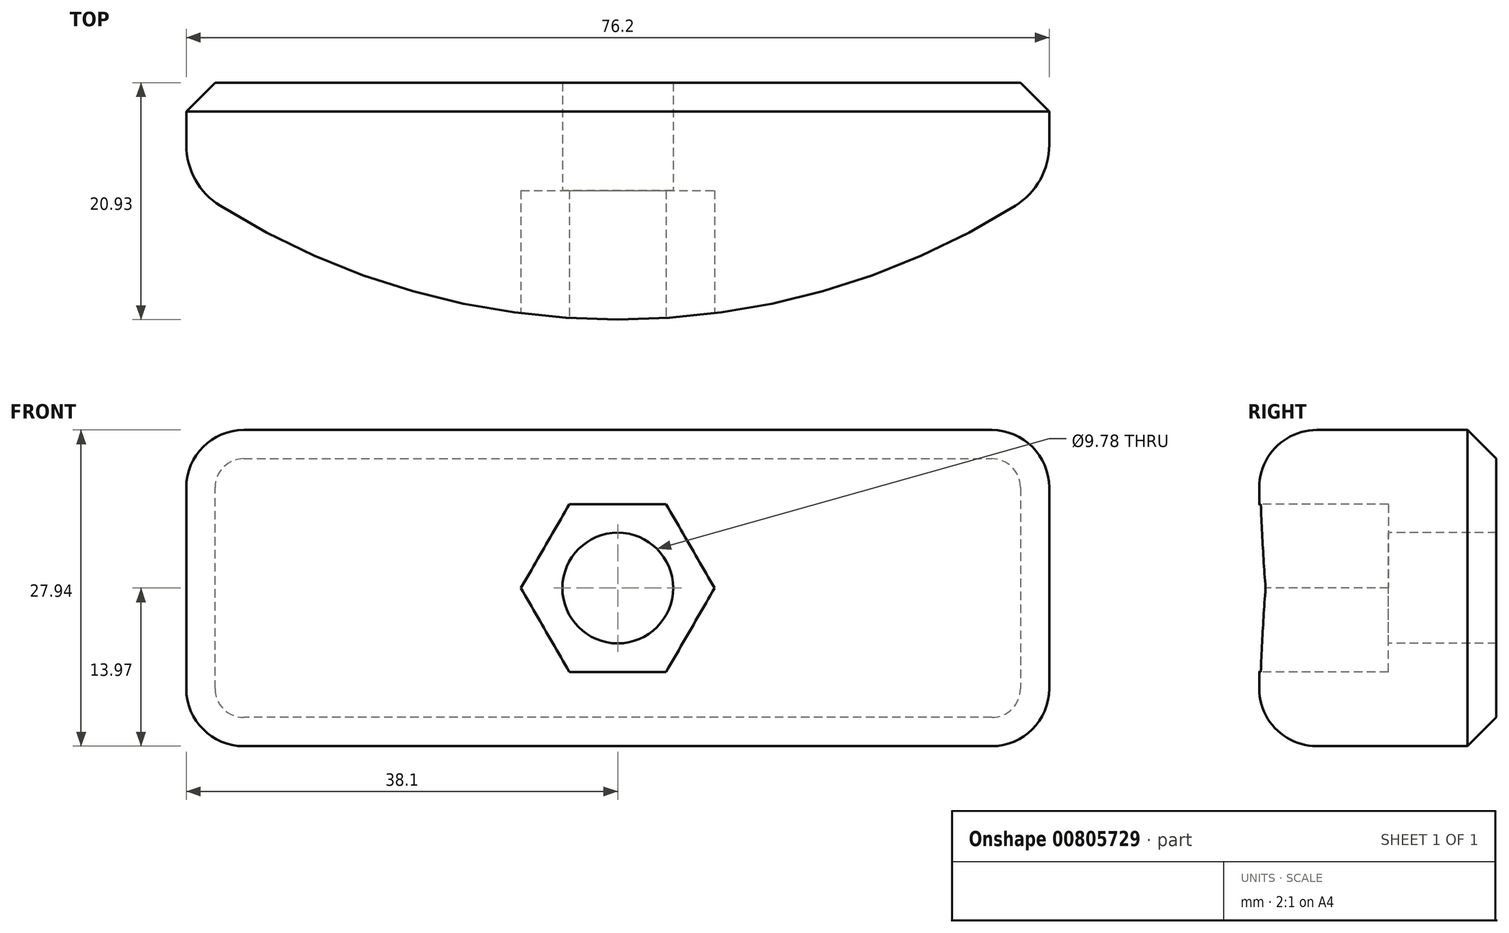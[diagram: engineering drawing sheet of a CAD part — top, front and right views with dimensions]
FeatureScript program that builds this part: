
annotation { "Feature Type Name" : "Feature", "Feature Type Description" : "" }
export const myFeature = defineFeature(function(context is Context, id is Id, definition is map)
    precondition{}
    {
        {
            var Q0;
            Q0=qCreatedBy(makeId("Front.planeOp"),FACE);
            var sketch = newSketch(context, id + "F0", { "sketchPlane" : qUnion([Q0])});
            skCircle(sketch, "E0", {"center": v(0, 0) * mm, "radius": 4.76 * mm});
            skSolve(sketch);
        }
        {
            var Q0;
            Q0 = qSketchRegion(id + "F0", true);
            extrude(context, id + "F1", {"entities" : qUnion([Q0]), "oppositeDirection" : true, "depth" : 254 * mm, "offsetDistance" : 25.4 * mm});
        }
        {
            var Q0;
            Q0=makeQuery(id+"F1.opExtrude","CAP_EDGE",EDGE,{"disambiguationData":[OSD([sQuery(id+"F0.wireOp",EDGE,"E0")])],"isStart":false});
            chamfer(context, id + "F2", {"entities" : qUnion([Q0]), "chamferType" : ChamferType.OFFSET_ANGLE, "width" : 6.35 * mm, "oppositeDirection" : false, "angle" : 15 * degree, "tangentPropagation" : true});
        }
        {
            var Q0;
            Q0=qCreatedBy(makeId("Top.planeOp"),FACE);
            var sketch = newSketch(context, id + "F3", { "sketchPlane" : qUnion([Q0])});
            skArc(sketch, "E1", {"start": v(-38.1, -8.9) * mm, "mid": v(0, -20.93) * mm, "end": v(38.1, -8.89) * mm});
            skLineSegment(sketch, "E2", {"start": v(38.1, -8.9) * mm, "end": v(38.1, 0) * mm});
            skLineSegment(sketch, "E3", {"start": v(38.1, 0) * mm, "end": v(-38.1, 0) * mm});
            skLineSegment(sketch, "E4", {"start": v(-38.1, 0) * mm, "end": v(-38.1, -8.9) * mm});
            skSolve(sketch);
        }
        {
            var Q0;
            Q0 = qSketchRegion(id + "F3", true);
            extrude(context, id + "F4", {"entities" : qUnion([Q0]), "depth" : 27.94 * mm, "offsetDistance" : 25.4 * mm, "symmetric" : true});
        }
        {
            var Q0;
            Q0=qCreatedBy(makeId("Front.planeOp"),FACE);
            cPlane(context, id + "F5", {"entities" : qUnion([Q0]), "cplaneType" : CPlaneType.OFFSET, "offset" : 25.4 * mm, "width" : 152.4 * mm, "height" : 152.4 * mm});
        }
        {
            var Q0;
            Q0=qCreatedBy(id+"F5.planeOp",FACE);
            var sketch = newSketch(context, id + "F6", { "sketchPlane" : qUnion([Q0])});
            skCircle(sketch, "E5.cCircle", {"center": v(0, 0) * mm, "radius": 7.4 * mm, "construction": true});
            skLineSegment(sketch, "E5.0", {"start": v(4.27, 7.4) * mm, "end": v(8.55, 0) * mm});
            skLineSegment(sketch, "E5.1", {"start": v(8.55, 0) * mm, "end": v(4.27, -7.4) * mm});
            skLineSegment(sketch, "E5.2", {"start": v(4.27, -7.4) * mm, "end": v(-4.27, -7.4) * mm});
            skLineSegment(sketch, "E5.3", {"start": v(-4.27, -7.4) * mm, "end": v(-8.55, 0) * mm});
            skLineSegment(sketch, "E5.4", {"start": v(-8.55, 0) * mm, "end": v(-4.27, 7.4) * mm});
            skLineSegment(sketch, "E5.5", {"start": v(-4.27, 7.4) * mm, "end": v(4.27, 7.4) * mm});
            skPoint(sketch, "E5.0.midPoint", {"position": v(6.41, 3.7) * mm});
            skSolve(sketch);
        }
        {
            var Q0;
            Q0=makeQuery(id+"F6.imprint","IMPRINT",FACE,{"disambiguationData":[TD([[makeQuery(id+"F6.imprint","IMPRINT",EDGE,{"derivedFrom":sQuery(id+"F6.wireOp",EDGE,"aEbGgsKV-B5vp-5zU8-L5dw-G5t5NTBtnHty")}),1.0]])]});
            var Q1;
            Q1=makeQuery(id+"F6.imprint","IMPRINT",FACE,{"disambiguationData":[TD([[makeQuery(id+"F6.imprint","IMPRINT",EDGE,{"derivedFrom":sQuery(id+"F6.wireOp",EDGE,"E5.0")}),-1.0]])]});
            extrude(context, id + "F7", {"entities" : qUnion([Q0, Q1]), "operationType" : NewBodyOperationType.REMOVE, "oppositeDirection" : true, "depth" : 15.88 * mm, "offsetDistance" : 25.4 * mm});
        }
        {
            var Q0;
            Q0=makeQuery(id+"F4.opExtrude","SWEPT_EDGE",EDGE,{"disambiguationData":[OSD([sQuery(id+"F3.wireOp",EDGE,"E1"),sQuery(id+"F3.wireOp",EDGE,"E2")])]});
            var Q1;
            Q1=makeQuery(id+"F4.opExtrude","SWEPT_EDGE",EDGE,{"disambiguationData":[OSD([sQuery(id+"F3.wireOp",EDGE,"E1"),sQuery(id+"F3.wireOp",EDGE,"E4")])]});
            fillet(context, id + "F8", {"entities" : qUnion([Q0, Q1]), "radius" : 6.35 * mm, "tangentPropagation" : true, "allowEdgeOverflow" : false});
        }
        {
            var Q0;
            Q0=makeQuery(id+"F7.boolean.opBoolean","COPY",FACE,{"derivedFrom":makeQuery(id+"F7.opExtrude","CAP_FACE",FACE,{"disambiguationData":[OSD([sQuery(id+"F6.wireOp",EDGE,"E5.0"),sQuery(id+"F6.wireOp",EDGE,"E5.1"),sQuery(id+"F6.wireOp",EDGE,"E5.2"),sQuery(id+"F6.wireOp",EDGE,"E5.3"),sQuery(id+"F6.wireOp",EDGE,"E5.4"),sQuery(id+"F6.wireOp",EDGE,"E5.5")])],"isStart":false})});
            var sketch = newSketch(context, id + "F9", { "sketchPlane" : qUnion([Q0])});
            skCircle(sketch, "E6", {"center": v(0, 0) * mm, "radius": 4.89 * mm});
            skSolve(sketch);
        }
        {
            var Q0;
            Q0 = qSketchRegion(id + "F9", true);
            extrude(context, id + "F10", {"entities" : qUnion([Q0]), "operationType" : NewBodyOperationType.REMOVE, "endBound" : BoundingType.THROUGH_ALL, "oppositeDirection" : true, "depth" : 25.4 * mm, "offsetDistance" : 25.4 * mm});
        }
        {
            var Q0;
            Q0=makeQuery(id+"F4.opExtrude","CAP_EDGE",EDGE,{"disambiguationData":[OSD([sQuery(id+"F3.wireOp",EDGE,"E1")])],"isStart":true});
            var Q1;
            Q1=makeQuery(id+"F4.opExtrude","CAP_EDGE",EDGE,{"disambiguationData":[OSD([sQuery(id+"F3.wireOp",EDGE,"E1")])],"isStart":false});
            fillet(context, id + "F11", {"entities" : qUnion([Q0, Q1]), "radius" : 5.08 * mm, "tangentPropagation" : true, "allowEdgeOverflow" : false});
        }
        {
            var Q0;
            Q0=makeQuery(id+"F4.opExtrude","CAP_EDGE",EDGE,{"disambiguationData":[OSD([sQuery(id+"F3.wireOp",EDGE,"E3")])],"isStart":true});
            chamfer(context, id + "F12", {"entities" : qUnion([Q0]), "width" : 2.54 * mm, "tangentPropagation" : true});
        }
    });
